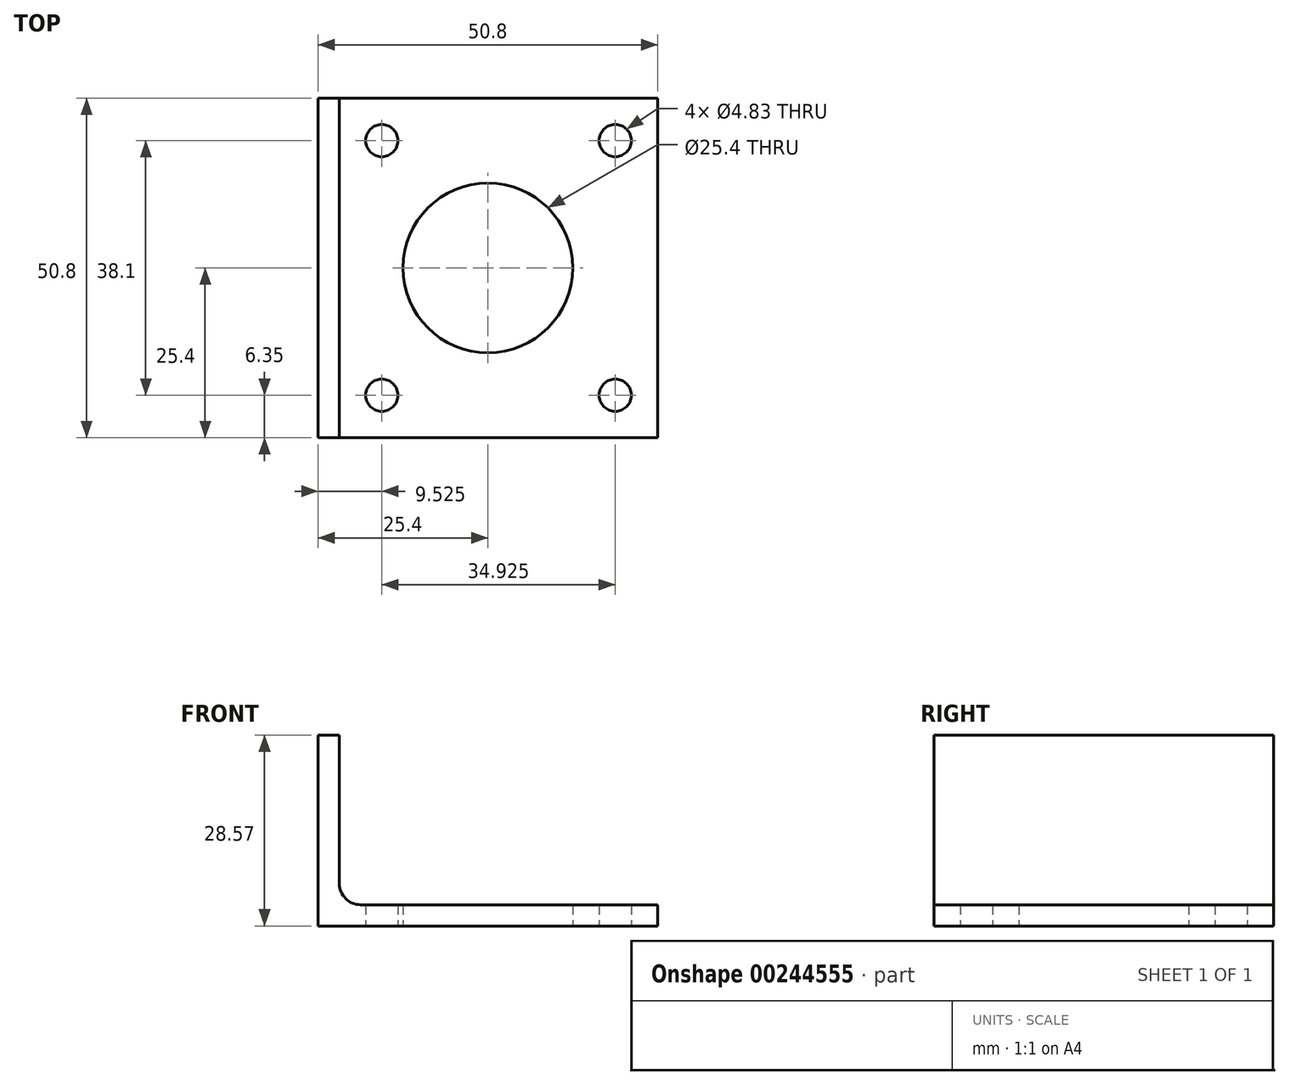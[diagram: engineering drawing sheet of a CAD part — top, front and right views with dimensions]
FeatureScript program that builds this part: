
annotation { "Feature Type Name" : "Feature", "Feature Type Description" : "" }
export const myFeature = defineFeature(function(context is Context, id is Id, definition is map)
    precondition{}
    {
        {
            var Q0;
            Q0=qCreatedBy(makeId("Front.planeOp"),FACE);
            var sketch = newSketch(context, id + "F0", { "sketchPlane" : qUnion([Q0])});
            skLineSegment(sketch, "E0", {"start": v(0, 0) * mm, "end": v(50.8, 0) * mm});
            skLineSegment(sketch, "E1", {"start": v(50.8, 0) * mm, "end": v(50.8, 3.18) * mm});
            skLineSegment(sketch, "E2", {"start": v(50.8, 3.18) * mm, "end": v(6.35, 3.18) * mm});
            skLineSegment(sketch, "E3", {"start": v(3.18, 6.35) * mm, "end": v(3.18, 28.57) * mm});
            skLineSegment(sketch, "E4", {"start": v(3.18, 28.57) * mm, "end": v(0, 28.57) * mm});
            skLineSegment(sketch, "E5", {"start": v(0, 28.57) * mm, "end": v(0, 0) * mm});
            skPoint(sketch, "E6.visualSharp", {"position": v(3.18, 3.18) * mm});
            skArc(sketch, "E6.filletArc", {"start": v(3.18, 6.35) * mm, "mid": v(4.1, 4.1) * mm, "end": v(6.35, 3.17) * mm});
            skSolve(sketch);
        }
        {
            var Q0;
            Q0=makeQuery(id+"F0.imprint","IMPRINT",FACE,{"disambiguationData":[TD([[makeQuery(id+"F0.imprint","IMPRINT",EDGE,{"derivedFrom":sQuery(id+"F0.wireOp",EDGE,"E0")}),1.0]])]});
            extrude(context, id + "F1", {"entities" : qUnion([Q0]), "depth" : 50.8 * mm});
        }
        {
            var Q0;
            Q0=makeQuery(id+"F1.opExtrude","SWEPT_FACE",FACE,{"disambiguationData":[OSD([sQuery(id+"F0.wireOp",EDGE,"E0")])]});
            var sketch = newSketch(context, id + "F2", { "sketchPlane" : qUnion([Q0])});
            skLineSegment(sketch, "E7", {"start": v(0, 50.8) * mm, "end": v(50.8, 0) * mm, "construction": true});
            skLineSegment(sketch, "E8", {"start": v(50.8, 50.8) * mm, "end": v(0, 0) * mm, "construction": true});
            skCircle(sketch, "E9", {"center": v(25.4, 25.4) * mm, "radius": 12.7 * mm});
            skLineSegment(sketch, "E10.0.0", {"start": v(0, 0) * mm, "end": v(50.8, 0) * mm, "construction": true});
            skLineSegment(sketch, "E10.0.1", {"start": v(50.8, 0) * mm, "end": v(50.8, 50.8) * mm, "construction": true});
            skLineSegment(sketch, "E10.0.2", {"start": v(50.8, 50.8) * mm, "end": v(0, 50.8) * mm, "construction": true});
            skLineSegment(sketch, "E10.0.3", {"start": v(0, 50.8) * mm, "end": v(0, 0) * mm, "construction": true});
            skLineSegment(sketch, "E11.0", {"start": v(44.45, 0) * mm, "end": v(44.45, 50.8) * mm, "construction": true});
            skLineSegment(sketch, "E12.0", {"start": v(50.8, 44.45) * mm, "end": v(0, 44.45) * mm, "construction": true});
            skLineSegment(sketch, "E13.0", {"start": v(9.53, 50.8) * mm, "end": v(9.53, 0) * mm, "construction": true});
            skLineSegment(sketch, "E14.0", {"start": v(0, 6.35) * mm, "end": v(50.8, 6.35) * mm, "construction": true});
            skCircle(sketch, "E15", {"center": v(44.45, 44.45) * mm, "radius": 2.41 * mm});
            skCircle(sketch, "E16", {"center": v(44.45, 6.35) * mm, "radius": 2.41 * mm});
            skCircle(sketch, "E17", {"center": v(9.53, 44.45) * mm, "radius": 2.41 * mm});
            skCircle(sketch, "E18", {"center": v(9.53, 6.35) * mm, "radius": 2.41 * mm});
            skSolve(sketch);
        }
        {
            var Q0;
            Q0=makeQuery(id+"F2.imprint","IMPRINT",FACE,{"disambiguationData":[TD([[makeQuery(id+"F2.imprint","IMPRINT",EDGE,{"derivedFrom":sQuery(id+"F2.wireOp",EDGE,"E15")}),1.0]])]});
            var Q1;
            Q1=makeQuery(id+"F2.imprint","IMPRINT",FACE,{"disambiguationData":[TD([[makeQuery(id+"F2.imprint","IMPRINT",EDGE,{"derivedFrom":sQuery(id+"F2.wireOp",EDGE,"E16")}),1.0]])]});
            var Q2;
            Q2=makeQuery(id+"F2.imprint","IMPRINT",FACE,{"disambiguationData":[TD([[makeQuery(id+"F2.imprint","IMPRINT",EDGE,{"derivedFrom":sQuery(id+"F2.wireOp",EDGE,"E9")}),1.0]])]});
            var Q3;
            Q3=makeQuery(id+"F2.imprint","IMPRINT",FACE,{"disambiguationData":[TD([[makeQuery(id+"F2.imprint","IMPRINT",EDGE,{"derivedFrom":sQuery(id+"F2.wireOp",EDGE,"E18")}),1.0]])]});
            var Q4;
            Q4=makeQuery(id+"F2.imprint","IMPRINT",FACE,{"disambiguationData":[TD([[makeQuery(id+"F2.imprint","IMPRINT",EDGE,{"derivedFrom":sQuery(id+"F2.wireOp",EDGE,"E17")}),1.0]])]});
            var Q5;
            Q5=sQuery(id+"F2.wireOp",EDGE,"E15");
            var Q6;
            Q6=sQuery(id+"F2.wireOp",EDGE,"E9");
            var Q7;
            Q7=sQuery(id+"F2.wireOp",EDGE,"E16");
            var Q8;
            Q8=sQuery(id+"F2.wireOp",EDGE,"E18");
            var Q9;
            Q9=sQuery(id+"F2.wireOp",EDGE,"E17");
            extrude(context, id + "F3", {"entities" : qUnion([Q0, Q1, Q2, Q3, Q4]), "operationType" : NewBodyOperationType.REMOVE, "surfaceEntities" : qUnion([Q5, Q6, Q7, Q8, Q9]), "endBound" : BoundingType.UP_TO_NEXT, "oppositeDirection" : true, "depth" : 25.4 * mm});
        }
    });
